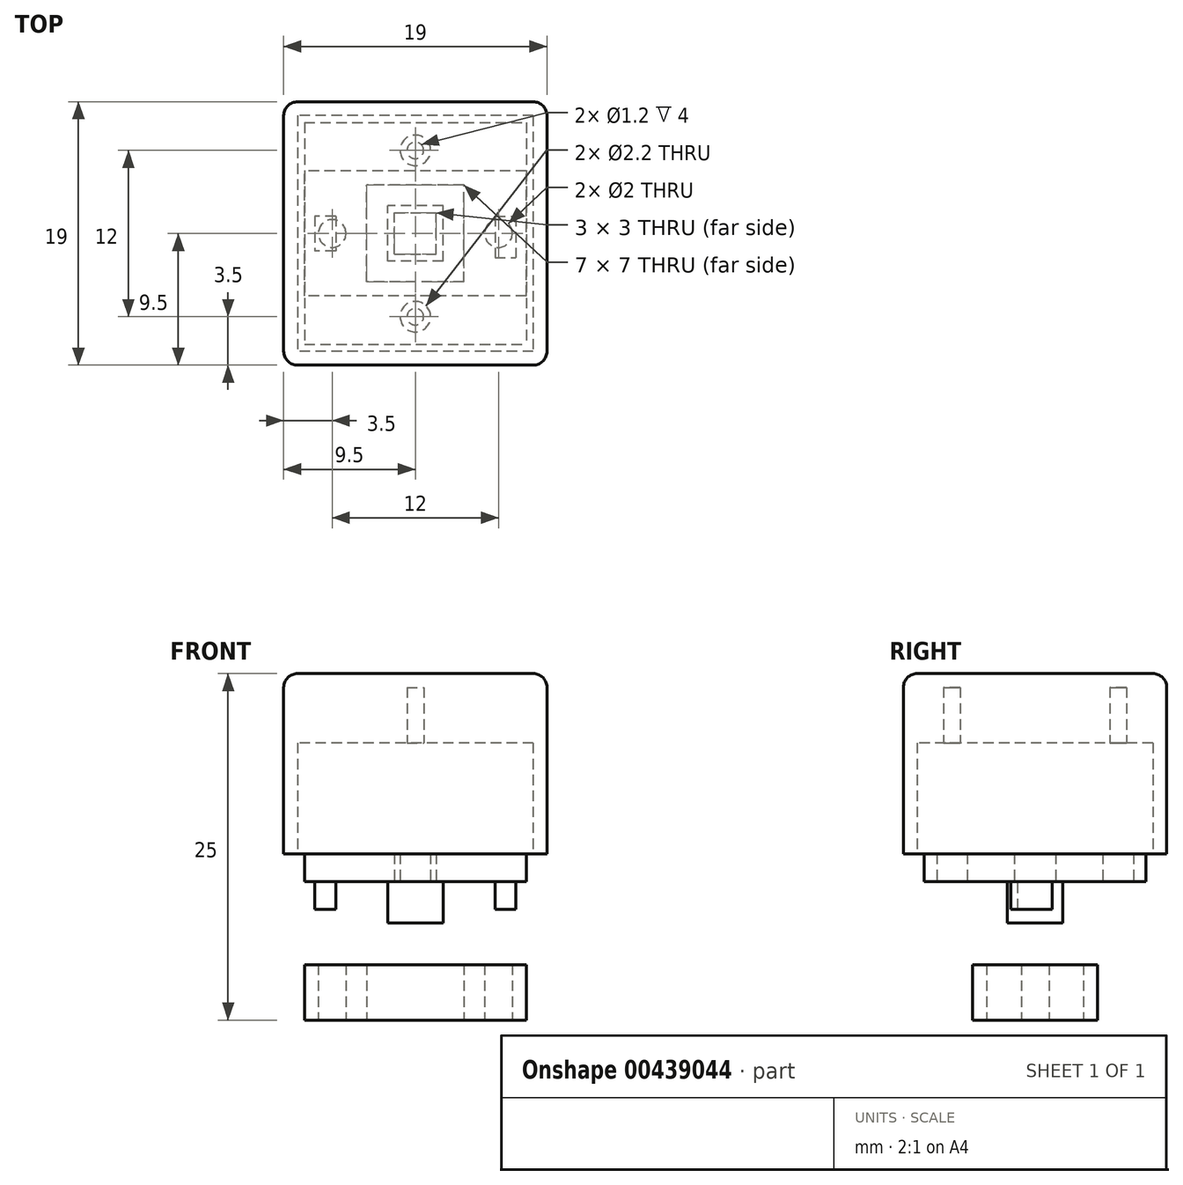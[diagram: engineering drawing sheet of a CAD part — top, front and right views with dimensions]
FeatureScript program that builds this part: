
annotation { "Feature Type Name" : "Feature", "Feature Type Description" : "" }
export const myFeature = defineFeature(function(context is Context, id is Id, definition is map)
    precondition{}
    {
        {
            var Q0;
            Q0=qCreatedBy(makeId("Top.planeOp"),FACE);
            var sketch = newSketch(context, id + "F0", { "sketchPlane" : qUnion([Q0])});
            skLineSegment(sketch, "E0.bottom", {"start": v(3.5, -3.5) * mm, "end": v(-3.5, -3.5) * mm});
            skLineSegment(sketch, "E0.top", {"start": v(3.5, 3.5) * mm, "end": v(-3.5, 3.5) * mm});
            skLineSegment(sketch, "E0.left", {"start": v(3.5, -3.5) * mm, "end": v(3.5, 3.5) * mm});
            skLineSegment(sketch, "E0.right", {"start": v(-3.5, -3.5) * mm, "end": v(-3.5, 3.5) * mm});
            skPoint(sketch, "E0.middle", {"position": v(0, 0) * mm});
            skLineSegment(sketch, "E1.bottom", {"start": v(8, -4.5) * mm, "end": v(-8, -4.5) * mm});
            skLineSegment(sketch, "E1.top", {"start": v(8, 4.5) * mm, "end": v(-8, 4.5) * mm});
            skLineSegment(sketch, "E1.left", {"start": v(8, -4.5) * mm, "end": v(8, 4.5) * mm});
            skLineSegment(sketch, "E1.right", {"start": v(-8, -4.5) * mm, "end": v(-8, 4.5) * mm});
            skCircle(sketch, "E2", {"center": v(-6, 0) * mm, "radius": 1 * mm});
            skCircle(sketch, "E3", {"center": v(6, 0) * mm, "radius": 1 * mm});
            skSolve(sketch);
        }
        {
            var Q0;
            Q0=qSketchRegion(id+"F0",true);
            extrude(context, id + "F1", {"entities" : qUnion([Q0]), "depth" : 4 * mm});
        }
        {
            var Q0;
            Q0=qCreatedBy(makeId("Top.planeOp"),FACE);
            cPlane(context, id + "F2", {"entities" : qUnion([Q0]), "cplaneType" : CPlaneType.OFFSET, "offset" : 10 * mm, "width" : 150 * mm, "height" : 150 * mm});
        }
        {
            var Q0;
            Q0=qCreatedBy(id+"F2.planeOp",FACE);
            var sketch = newSketch(context, id + "F3", { "sketchPlane" : qUnion([Q0])});
            skLineSegment(sketch, "E4.bottom", {"start": v(2, -2) * mm, "end": v(-2, -2) * mm});
            skLineSegment(sketch, "E4.top", {"start": v(2, 2) * mm, "end": v(-2, 2) * mm});
            skLineSegment(sketch, "E4.left", {"start": v(2, -2) * mm, "end": v(2, 2) * mm});
            skLineSegment(sketch, "E4.right", {"start": v(-2, -2) * mm, "end": v(-2, 2) * mm});
            skPoint(sketch, "E4.middle", {"position": v(0, 0) * mm});
            skSolve(sketch);
        }
        {
            var Q0;
            Q0=qSketchRegion(id+"F3",true);
            extrude(context, id + "F4", {"entities" : qUnion([Q0]), "oppositeDirection" : true, "depth" : 3 * mm});
        }
        {
            var Q0;
            Q0=qCreatedBy(id+"F2.planeOp",FACE);
            var sketch = newSketch(context, id + "F5", { "sketchPlane" : qUnion([Q0])});
            skLineSegment(sketch, "E5.bottom", {"start": v(8, -8) * mm, "end": v(-8, -8) * mm});
            skLineSegment(sketch, "E5.top", {"start": v(8, 8) * mm, "end": v(-8, 8) * mm});
            skLineSegment(sketch, "E5.left", {"start": v(8, -8) * mm, "end": v(8, 8) * mm});
            skLineSegment(sketch, "E5.right", {"start": v(-8, -8) * mm, "end": v(-8, 8) * mm});
            skPoint(sketch, "E5.middle", {"position": v(0, 0) * mm});
            skCircle(sketch, "E6", {"center": v(0, -6) * mm, "radius": 1.1 * mm});
            skCircle(sketch, "E7", {"center": v(0, 6) * mm, "radius": 1.1 * mm});
            skLineSegment(sketch, "E8.bottom", {"start": v(1.5, 1.5) * mm, "end": v(-1.5, 1.5) * mm});
            skLineSegment(sketch, "E8.top", {"start": v(1.5, -1.5) * mm, "end": v(-1.5, -1.5) * mm});
            skLineSegment(sketch, "E8.left", {"start": v(1.5, 1.5) * mm, "end": v(1.5, -1.5) * mm});
            skLineSegment(sketch, "E8.right", {"start": v(-1.5, 1.5) * mm, "end": v(-1.5, -1.5) * mm});
            skSolve(sketch);
        }
        {
            var Q0;
            Q0=qSketchRegion(id+"F5",true);
            extrude(context, id + "F6", {"entities" : qUnion([Q0]), "depth" : 3 * mm});
        }
        {
            var Q0;
            Q0=qCreatedBy(makeId("Top.planeOp"),FACE);
            cPlane(context, id + "F7", {"entities" : qUnion([Q0]), "cplaneType" : CPlaneType.OFFSET, "offset" : 12 * mm, "width" : 150 * mm, "height" : 150 * mm});
        }
        {
            var Q0;
            Q0=qCreatedBy(id+"F7.planeOp",FACE);
            var sketch = newSketch(context, id + "F8", { "sketchPlane" : qUnion([Q0])});
            skLineSegment(sketch, "E9.bottom", {"start": v(9.5, -9.5) * mm, "end": v(-9.5, -9.5) * mm});
            skLineSegment(sketch, "E9.top", {"start": v(9.5, 9.5) * mm, "end": v(-9.5, 9.5) * mm});
            skLineSegment(sketch, "E9.left", {"start": v(9.5, -9.5) * mm, "end": v(9.5, 9.5) * mm});
            skLineSegment(sketch, "E9.right", {"start": v(-9.5, -9.5) * mm, "end": v(-9.5, 9.5) * mm});
            skPoint(sketch, "E9.middle", {"position": v(0, 0) * mm});
            skSolve(sketch);
        }
        {
            var Q0;
            Q0=qSketchRegion(id+"F8",true);
            extrude(context, id + "F9", {"entities" : qUnion([Q0]), "depth" : 13 * mm});
        }
        {
            var Q0;
            Q0=makeQuery(id+"F9.opExtrude","CAP_FACE",FACE,{"disambiguationData":[OSD([sQuery(id+"F8.wireOp",EDGE,"E9.bottom"),sQuery(id+"F8.wireOp",EDGE,"E9.top"),sQuery(id+"F8.wireOp",EDGE,"E9.left"),sQuery(id+"F8.wireOp",EDGE,"E9.right")])],"isStart":true});
            var sketch = newSketch(context, id + "F10", { "sketchPlane" : qUnion([Q0])});
            skLineSegment(sketch, "E10.bottom", {"start": v(8.5, -8.5) * mm, "end": v(-8.5, -8.5) * mm});
            skLineSegment(sketch, "E10.top", {"start": v(8.5, 8.5) * mm, "end": v(-8.5, 8.5) * mm});
            skLineSegment(sketch, "E10.left", {"start": v(8.5, -8.5) * mm, "end": v(8.5, 8.5) * mm});
            skLineSegment(sketch, "E10.right", {"start": v(-8.5, -8.5) * mm, "end": v(-8.5, 8.5) * mm});
            skPoint(sketch, "E10.middle", {"position": v(0, 0) * mm});
            skSolve(sketch);
        }
        {
            var Q0;
            Q0=qSketchRegion(id+"F10",true);
            extrude(context, id + "F11", {"entities" : qUnion([Q0]), "operationType" : NewBodyOperationType.REMOVE, "oppositeDirection" : true, "depth" : 8 * mm});
        }
        {
            var Q0;
            Q0=makeQuery(id+"F11.boolean.opBoolean","COPY",FACE,{"derivedFrom":makeQuery(id+"F11.opExtrude","CAP_FACE",FACE,{"disambiguationData":[OSD([sQuery(id+"F10.wireOp",EDGE,"E10.bottom"),sQuery(id+"F10.wireOp",EDGE,"E10.top"),sQuery(id+"F10.wireOp",EDGE,"E10.left"),sQuery(id+"F10.wireOp",EDGE,"E10.right")])],"isStart":false})});
            var sketch = newSketch(context, id + "F12", { "sketchPlane" : qUnion([Q0])});
            skCircle(sketch, "E11", {"center": v(0, 6) * mm, "radius": 0.6 * mm});
            skCircle(sketch, "E12", {"center": v(0, -6) * mm, "radius": 0.6 * mm});
            skSolve(sketch);
        }
        {
            var Q0;
            Q0=qSketchRegion(id+"F12",true);
            extrude(context, id + "F13", {"entities" : qUnion([Q0]), "operationType" : NewBodyOperationType.REMOVE, "oppositeDirection" : true, "depth" : 4 * mm});
        }
        {
            var Q0;
            Q0=makeQuery(id+"F9.opExtrude","SWEPT_EDGE",EDGE,{"disambiguationData":[OSD([sQuery(id+"F8.wireOp",EDGE,"E9.bottom"),sQuery(id+"F8.wireOp",EDGE,"E9.right")])]});
            var Q1;
            Q1=makeQuery(id+"F9.opExtrude","SWEPT_EDGE",EDGE,{"disambiguationData":[OSD([sQuery(id+"F8.wireOp",EDGE,"E9.bottom"),sQuery(id+"F8.wireOp",EDGE,"E9.left")])]});
            var Q2;
            Q2=makeQuery(id+"F9.opExtrude","SWEPT_EDGE",EDGE,{"disambiguationData":[OSD([sQuery(id+"F8.wireOp",EDGE,"E9.top"),sQuery(id+"F8.wireOp",EDGE,"E9.right")])]});
            var Q3;
            Q3=makeQuery(id+"F9.opExtrude","SWEPT_EDGE",EDGE,{"disambiguationData":[OSD([sQuery(id+"F8.wireOp",EDGE,"E9.top"),sQuery(id+"F8.wireOp",EDGE,"E9.left")])]});
            var Q4;
            Q4=makeQuery(id+"F9.opExtrude","CAP_FACE",FACE,{"disambiguationData":[OSD([sQuery(id+"F8.wireOp",EDGE,"E9.bottom"),sQuery(id+"F8.wireOp",EDGE,"E9.top"),sQuery(id+"F8.wireOp",EDGE,"E9.left"),sQuery(id+"F8.wireOp",EDGE,"E9.right")])],"isStart":false});
            fillet(context, id + "F14", {"entities" : qUnion([Q0, Q1, Q2, Q3, Q4]), "radius" : 1 * mm, "tangentPropagation" : true, "allowEdgeOverflow" : false});
        }
        {
            var Q0;
            Q0=makeQuery(id+"F6.opExtrude","CAP_FACE",FACE,{"disambiguationData":[OSD([sQuery(id+"F5.wireOp",EDGE,"E5.bottom"),sQuery(id+"F5.wireOp",EDGE,"E5.top"),sQuery(id+"F5.wireOp",EDGE,"E5.left"),sQuery(id+"F5.wireOp",EDGE,"E5.right"),sQuery(id+"F5.wireOp",EDGE,"E6"),sQuery(id+"F5.wireOp",EDGE,"E7")])],"isStart":true});
            var sketch = newSketch(context, id + "F15", { "sketchPlane" : qUnion([Q0])});
            skLineSegment(sketch, "E13.bottom", {"start": v(5.75, -1.25) * mm, "end": v(7.25, -1.25) * mm});
            skLineSegment(sketch, "E13.top", {"start": v(5.75, 1.75) * mm, "end": v(7.25, 1.75) * mm});
            skLineSegment(sketch, "E13.left", {"start": v(5.75, -1.25) * mm, "end": v(5.75, 1.75) * mm});
            skLineSegment(sketch, "E13.right", {"start": v(7.25, -1.25) * mm, "end": v(7.25, 1.75) * mm});
            skPoint(sketch, "E13.middle", {"position": v(6.5, 0.25) * mm});
            skLineSegment(sketch, "E14.bottom", {"start": v(-5.75, -1.25) * mm, "end": v(-7.25, -1.25) * mm});
            skLineSegment(sketch, "E14.top", {"start": v(-5.75, 1.25) * mm, "end": v(-7.25, 1.25) * mm});
            skLineSegment(sketch, "E14.left", {"start": v(-5.75, -1.25) * mm, "end": v(-5.75, 1.25) * mm});
            skLineSegment(sketch, "E14.right", {"start": v(-7.25, -1.25) * mm, "end": v(-7.25, 1.25) * mm});
            skPoint(sketch, "E14.middle", {"position": v(-6.5, 0) * mm});
            skPoint(sketch, "E14.middle.positionSnap0", {"position": v(-1.5, 0) * mm});
            skPoint(sketch, "E14.cornerSnap0", {"position": v(6.5, -1.25) * mm});
            skPoint(sketch, "E14.centerSnap0", {"position": v(-1.5, 0) * mm});
            skSolve(sketch);
        }
        {
            var Q0;
            Q0=qSketchRegion(id+"F15",true);
            extrude(context, id + "F16", {"entities" : qUnion([Q0]), "operationType" : NewBodyOperationType.ADD, "depth" : 2 * mm});
        }
    });
